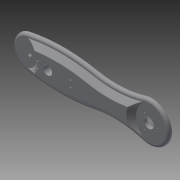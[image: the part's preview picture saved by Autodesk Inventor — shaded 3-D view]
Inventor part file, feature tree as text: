
AUTODESK INVENTOR PART (.ipt)
format: ipt  version: 2015 (Build 190159000, 159)  size: 408,064 bytes
history: native  units: mm
features: sketch x11, extrude x8, fillet x2, chamfer x1
ambient origin geometry x8: Origin, YZ Plane, XZ Plane, XY Plane, X Axis, Y Axis, Z Axis, Center Point
bodies: Solid1 (feature_tree)
feature tree (22):
  extrude  "Extrusion1"  Depth=50.0mm
  extrude  "Extrusion2"  Depth=5.0mm
  extrude  "Extrusion3"  Depth=5.0mm TaperAngle=0.0deg
  extrude  "Extrusion4"  Depth=18.1mm
  extrude  "Extrusion5"  Depth=20.0mm
  extrude  "Extrusion6"  Depth=9.5mm
  sketch  "Sketch7"  dims[d15=9.9mm d16=9.5mm]
  extrude  "Extrusion7"  Depth=9.5mm
  extrude  "Extrusion13"  Depth=3.0mm
  sketch  "Sketch15"  dims[d20=3.0mm]
  chamfer  "Chamfer2"  Distance=13.6mm
  sketch  "Sketch16"  dims[d21=3.0mm d22=13.6mm d23=5.0mm d24=0.0mm d26=2.0mm d29=2.0mm d30=2.0mm d31=5.0mm d32=0.0mm d63=5.0mm d64=0.0mm d65=5.0mm d66=0.0mm d72=20.0mm d73=30.0mm d74=7.3mm d75=0.0mm d103=6.0mm d104=5.0mm d105=0.0mm d106=7.3mm d107=2.0mm d108=45.0deg d109=1.0mm d111=4.0mm]
  fillet  "Fillet1"  Radius=5.0mm
  fillet  "Fillet3"  Radius=2.0mm
  sketch  "Sketch1"  dims[d0=180.0mm d1=50.0mm]
  sketch  "Sketch2"  dims[d2=5.0mm d3=0.0mm d4=15.0mm]
  sketch  "Sketch3"  dims[d5=15.0mm d6=5.0mm d7=0.0mm]
  sketch  "Sketch4"  dims[d9=34.65mm d10=18.1mm]
  sketch  "Sketch5"  dims[d11=55.0mm d12=20.0mm]
  sketch  "Sketch6"  dims[d13=40.2mm d14=9.5mm]
  sketch  "Sketch8"  dims[d17=9.9mm d18=3.0mm]
  sketch  "Sketch14"  dims[d19=3.0mm]
